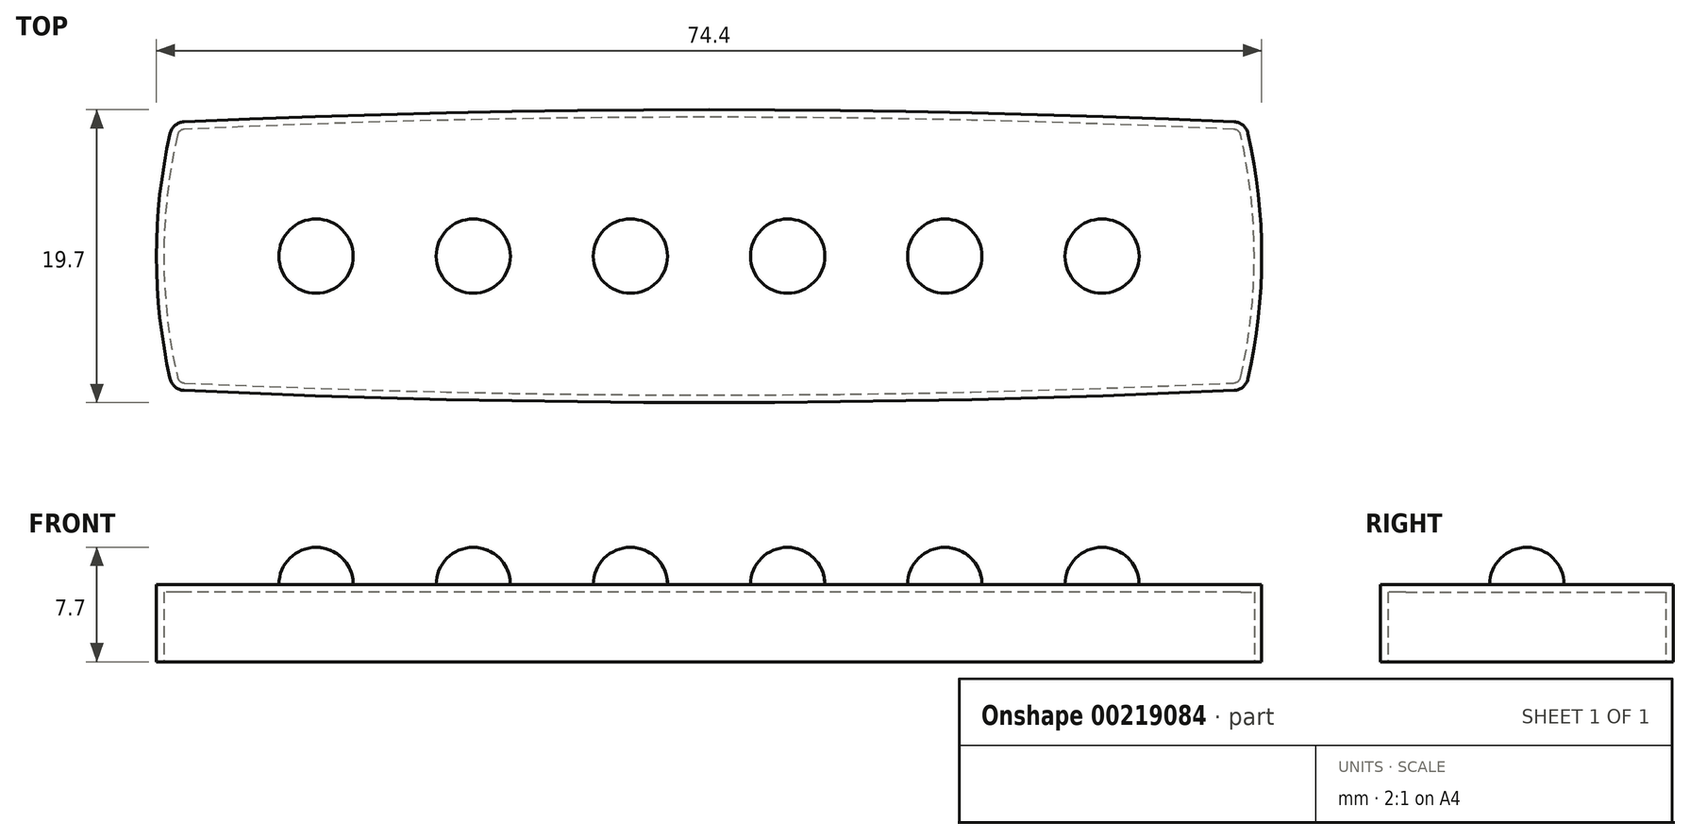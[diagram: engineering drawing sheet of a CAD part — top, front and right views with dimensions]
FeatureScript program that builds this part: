
annotation { "Feature Type Name" : "Feature", "Feature Type Description" : "" }
export const myFeature = defineFeature(function(context is Context, id is Id, definition is map)
    precondition{}
    {
        {
            var Q0;
            Q0=qCreatedBy(makeId("Top.planeOp"),FACE);
            var sketch = newSketch(context, id + "F0", { "sketchPlane" : qUnion([Q0])});
            skLineSegment(sketch, "E0", {"start": v(0, -9.85) * mm, "end": v(0, 9.85) * mm, "construction": true});
            skArc(sketch, "E1", {"start": v(35.34, 9.04) * mm, "mid": v(0, 9.85) * mm, "end": v(-35.34, 9.04) * mm});
            skArc(sketch, "E2", {"start": v(-35.34, -9.04) * mm, "mid": v(0, -9.85) * mm, "end": v(35.34, -9.04) * mm});
            skPoint(sketch, "E3.visualSharp", {"position": v(36.1, 9) * mm});
            skPoint(sketch, "E4.visualSharp", {"position": v(36.1, -9) * mm});
            skLineSegment(sketch, "E5", {"start": v(-36.66, 9.85) * mm, "end": v(35.84, 9.85) * mm, "construction": true});
            skLineSegment(sketch, "E6", {"start": v(36.71, -9.85) * mm, "end": v(-35.61, -9.85) * mm, "construction": true});
            skArc(sketch, "E7", {"start": v(36.27, -8.26) * mm, "mid": v(37.2, 0) * mm, "end": v(36.27, 8.26) * mm});
            skArc(sketch, "E8.trimOffspring", {"start": v(-36.27, 8.26) * mm, "mid": v(-37.2, 0) * mm, "end": v(-36.27, -8.26) * mm});
            skPoint(sketch, "E9.visualSharp", {"position": v(-36.1, 9) * mm});
            skArc(sketch, "E9.filletArc", {"start": v(-35.34, 9.04) * mm, "mid": v(-35.94, 8.8) * mm, "end": v(-36.27, 8.26) * mm});
            skArc(sketch, "E10.filletArc", {"start": v(36.27, 8.26) * mm, "mid": v(35.94, 8.8) * mm, "end": v(35.34, 9.04) * mm});
            skArc(sketch, "E11.filletArc", {"start": v(35.34, -9.04) * mm, "mid": v(35.94, -8.8) * mm, "end": v(36.27, -8.26) * mm});
            skPoint(sketch, "E12.visualSharp", {"position": v(-36.1, -9) * mm});
            skArc(sketch, "E12.filletArc", {"start": v(-36.27, -8.26) * mm, "mid": v(-35.94, -8.8) * mm, "end": v(-35.34, -9.04) * mm});
            skSolve(sketch);
        }
        {
            var Q0;
            Q0 = qSketchRegion(id + "F0", true);
            extrude(context, id + "F1", {"entities" : qUnion([Q0]), "depth" : 5.2 * mm});
        }
        {
            var Q0;
            Q0=makeQuery(id+"F1.opExtrude","CAP_FACE",FACE,{"disambiguationData":[OSD([sQuery(id+"F0.wireOp",EDGE,"z8xfCGf6-fLwg-P1dX-434f-4KBh6KLLWTA6"),sQuery(id+"F0.wireOp",EDGE,"W8wgIIa4-ixdi-G1A6-SWh8-LI75K1CJTo1U"),sQuery(id+"F0.wireOp",EDGE,"E1"),sQuery(id+"F0.wireOp",EDGE,"E2"),sQuery(id+"F0.wireOp",EDGE,"e75bb580-8d87-4779-9360-eeb9e8da6317.filletArc"),sQuery(id+"F0.wireOp",EDGE,"E3.filletArc"),sQuery(id+"F0.wireOp",EDGE,"E4.filletArc"),sQuery(id+"F0.wireOp",EDGE,"76380c13-caca-47f1-bbc9-d40562fbe30c.filletArc")])],"isStart":true});
            shell(context, id + "F2", {"entities" : qUnion([Q0]), "thickness" : 0.5 * mm});
        }
        {
            var Q0;
            Q0=makeQuery(id+"F1.opExtrude","CAP_FACE",FACE,{"disambiguationData":[OSD([sQuery(id+"F0.wireOp",EDGE,"z8xfCGf6-fLwg-P1dX-434f-4KBh6KLLWTA6"),sQuery(id+"F0.wireOp",EDGE,"W8wgIIa4-ixdi-G1A6-SWh8-LI75K1CJTo1U"),sQuery(id+"F0.wireOp",EDGE,"E1"),sQuery(id+"F0.wireOp",EDGE,"E2"),sQuery(id+"F0.wireOp",EDGE,"e75bb580-8d87-4779-9360-eeb9e8da6317.filletArc"),sQuery(id+"F0.wireOp",EDGE,"E3.filletArc"),sQuery(id+"F0.wireOp",EDGE,"E4.filletArc"),sQuery(id+"F0.wireOp",EDGE,"76380c13-caca-47f1-bbc9-d40562fbe30c.filletArc")])],"isStart":false});
            var sketch = newSketch(context, id + "F3", { "sketchPlane" : qUnion([Q0])});
            skLineSegment(sketch, "E13", {"start": v(-37.2, 0) * mm, "end": v(37, 0) * mm, "construction": true});
            skLineSegment(sketch, "E14", {"start": v(0, 9.85) * mm, "end": v(0, -9.85) * mm, "construction": true});
            skLineSegment(sketch, "E15.0", {"start": v(-5.3, 9.83) * mm, "end": v(-5.3, -9.83) * mm, "construction": true});
            skLineSegment(sketch, "E16.0", {"start": v(5.29, 9.83) * mm, "end": v(5.29, -9.83) * mm, "construction": true});
            skLineSegment(sketch, "E17.0", {"start": v(15.87, 9.69) * mm, "end": v(15.87, -9.69) * mm, "construction": true});
            skLineSegment(sketch, "E18.0", {"start": v(26.45, 9.4) * mm, "end": v(26.45, -9.4) * mm, "construction": true});
            skLineSegment(sketch, "E19.0", {"start": v(-15.87, 9.69) * mm, "end": v(-15.87, -9.69) * mm, "construction": true});
            skLineSegment(sketch, "E20.0", {"start": v(-26.45, 9.4) * mm, "end": v(-26.45, -9.4) * mm, "construction": true});
            skPoint(sketch, "E21", {"position": v(-26.45, 0) * mm});
            skPoint(sketch, "E22", {"position": v(-15.87, 0) * mm});
            skPoint(sketch, "E23", {"position": v(-42.54, 6.05) * mm});
            skPoint(sketch, "E24", {"position": v(-5.29, 0) * mm});
            skPoint(sketch, "E25", {"position": v(5.3, 0) * mm});
            skPoint(sketch, "E26", {"position": v(15.87, 0) * mm});
            skPoint(sketch, "E27", {"position": v(26.45, 0) * mm});
            skSolve(sketch);
        }
        {
            var Q0;
            Q0=qCreatedBy(makeId("Front.planeOp"),FACE);
            var sketch = newSketch(context, id + "F4", { "sketchPlane" : qUnion([Q0])});
            skLineSegment(sketch, "E28", {"start": v(26.45, 5.2) * mm, "end": v(26.45, 10.2) * mm, "construction": true});
            skLineSegment(sketch, "E29", {"start": v(15.87, 5.2) * mm, "end": v(15.87, 10.2) * mm, "construction": true});
            skLineSegment(sketch, "E30", {"start": v(5.29, 5.2) * mm, "end": v(5.29, 10.2) * mm, "construction": true});
            skLineSegment(sketch, "E31", {"start": v(-5.3, 5.2) * mm, "end": v(-5.3, 10.2) * mm, "construction": true});
            skLineSegment(sketch, "E32", {"start": v(-15.87, 5.2) * mm, "end": v(-15.87, 10.2) * mm, "construction": true});
            skLineSegment(sketch, "E33", {"start": v(-26.45, 5.2) * mm, "end": v(-26.45, 10.2) * mm, "construction": true});
            skSolve(sketch);
        }
        {
            var Q0;
            Q0=qCreatedBy(makeId("Front.planeOp"),FACE);
            var sketch = newSketch(context, id + "F5", { "sketchPlane" : qUnion([Q0])});
            skArc(sketch, "E34", {"start": v(28.95, 5.2) * mm, "mid": v(28.22, 6.97) * mm, "end": v(26.45, 7.7) * mm});
            skLineSegment(sketch, "E35", {"start": v(26.45, 7.7) * mm, "end": v(26.45, 5.2) * mm});
            skLineSegment(sketch, "E36", {"start": v(26.45, 5.2) * mm, "end": v(28.95, 5.2) * mm});
            skArc(sketch, "E37", {"start": v(18.37, 5.2) * mm, "mid": v(17.64, 6.97) * mm, "end": v(15.87, 7.7) * mm});
            skLineSegment(sketch, "E38", {"start": v(15.87, 7.7) * mm, "end": v(15.87, 5.2) * mm});
            skLineSegment(sketch, "E39", {"start": v(15.87, 5.2) * mm, "end": v(18.37, 5.2) * mm});
            skArc(sketch, "E40", {"start": v(7.79, 5.2) * mm, "mid": v(7.06, 6.97) * mm, "end": v(5.3, 7.7) * mm});
            skLineSegment(sketch, "E41", {"start": v(5.3, 7.7) * mm, "end": v(5.3, 5.2) * mm});
            skLineSegment(sketch, "E42", {"start": v(5.29, 5.2) * mm, "end": v(7.79, 5.2) * mm});
            skArc(sketch, "E43", {"start": v(-2.8, 5.2) * mm, "mid": v(-3.52, 6.97) * mm, "end": v(-5.3, 7.7) * mm});
            skLineSegment(sketch, "E44", {"start": v(-5.3, 7.7) * mm, "end": v(-5.3, 5.2) * mm});
            skLineSegment(sketch, "E45", {"start": v(-5.3, 5.2) * mm, "end": v(-2.8, 5.2) * mm});
            skArc(sketch, "E46", {"start": v(-13.37, 5.2) * mm, "mid": v(-14.1, 6.97) * mm, "end": v(-15.87, 7.7) * mm});
            skLineSegment(sketch, "E47", {"start": v(-15.87, 7.7) * mm, "end": v(-15.87, 5.2) * mm});
            skLineSegment(sketch, "E48", {"start": v(-15.87, 5.2) * mm, "end": v(-13.37, 5.2) * mm});
            skArc(sketch, "E49", {"start": v(-23.95, 5.2) * mm, "mid": v(-24.68, 6.97) * mm, "end": v(-26.45, 7.7) * mm});
            skLineSegment(sketch, "E50", {"start": v(-26.45, 7.7) * mm, "end": v(-26.45, 5.2) * mm});
            skLineSegment(sketch, "E51", {"start": v(-26.45, 5.2) * mm, "end": v(-23.95, 5.2) * mm});
            skSolve(sketch);
        }
        {
            var Q0;
            Q0=makeQuery(id+"F5.imprint","IMPRINT",FACE,{"disambiguationData":[TD([[makeQuery(id+"F5.imprint","IMPRINT",EDGE,{"derivedFrom":sQuery(id+"F5.wireOp",EDGE,"E37")}),1.0]])]});
            var Q1;
            Q1=sQuery(id+"F4.wireOp",EDGE,"E29");
            revolve(context, id + "F6", {"operationType" : NewBodyOperationType.ADD, "entities" : qUnion([Q0]), "axis" : qUnion([Q1]), "revolveType" : RevolveType.FULL});
        }
        {
            var Q0;
            Q0=makeQuery(id+"F5.imprint","IMPRINT",FACE,{"disambiguationData":[TD([[makeQuery(id+"F5.imprint","IMPRINT",EDGE,{"derivedFrom":sQuery(id+"F5.wireOp",EDGE,"E49")}),1.0]])]});
            var Q1;
            Q1=sQuery(id+"F4.wireOp",EDGE,"E33");
            revolve(context, id + "F7", {"operationType" : NewBodyOperationType.ADD, "entities" : qUnion([Q0]), "axis" : qUnion([Q1]), "revolveType" : RevolveType.FULL});
        }
        {
            var Q0;
            Q0=makeQuery(id+"F5.imprint","IMPRINT",FACE,{"disambiguationData":[TD([[makeQuery(id+"F5.imprint","IMPRINT",EDGE,{"derivedFrom":sQuery(id+"F5.wireOp",EDGE,"E46")}),1.0]])]});
            var Q1;
            Q1=sQuery(id+"F4.wireOp",EDGE,"E32");
            revolve(context, id + "F8", {"operationType" : NewBodyOperationType.ADD, "entities" : qUnion([Q0]), "axis" : qUnion([Q1]), "revolveType" : RevolveType.FULL});
        }
        {
            var Q0;
            Q0=makeQuery(id+"F5.imprint","IMPRINT",FACE,{"disambiguationData":[TD([[makeQuery(id+"F5.imprint","IMPRINT",EDGE,{"derivedFrom":sQuery(id+"F5.wireOp",EDGE,"E43")}),1.0]])]});
            var Q1;
            Q1=sQuery(id+"F4.wireOp",EDGE,"E31");
            revolve(context, id + "F9", {"operationType" : NewBodyOperationType.ADD, "entities" : qUnion([Q0]), "axis" : qUnion([Q1]), "revolveType" : RevolveType.FULL});
        }
        {
            var Q0;
            Q0=makeQuery(id+"F5.imprint","IMPRINT",FACE,{"disambiguationData":[TD([[makeQuery(id+"F5.imprint","IMPRINT",EDGE,{"derivedFrom":sQuery(id+"F5.wireOp",EDGE,"E40")}),1.0]])]});
            var Q1;
            Q1=sQuery(id+"F4.wireOp",EDGE,"E30");
            revolve(context, id + "F10", {"operationType" : NewBodyOperationType.ADD, "entities" : qUnion([Q0]), "axis" : qUnion([Q1]), "revolveType" : RevolveType.FULL});
        }
        {
            var Q0;
            Q0=makeQuery(id+"F5.imprint","IMPRINT",FACE,{"disambiguationData":[TD([[makeQuery(id+"F5.imprint","IMPRINT",EDGE,{"derivedFrom":sQuery(id+"F5.wireOp",EDGE,"E34")}),1.0]])]});
            var Q1;
            Q1=sQuery(id+"F4.wireOp",EDGE,"E28");
            revolve(context, id + "F11", {"operationType" : NewBodyOperationType.ADD, "entities" : qUnion([Q0]), "axis" : qUnion([Q1]), "revolveType" : RevolveType.FULL});
        }
    });
